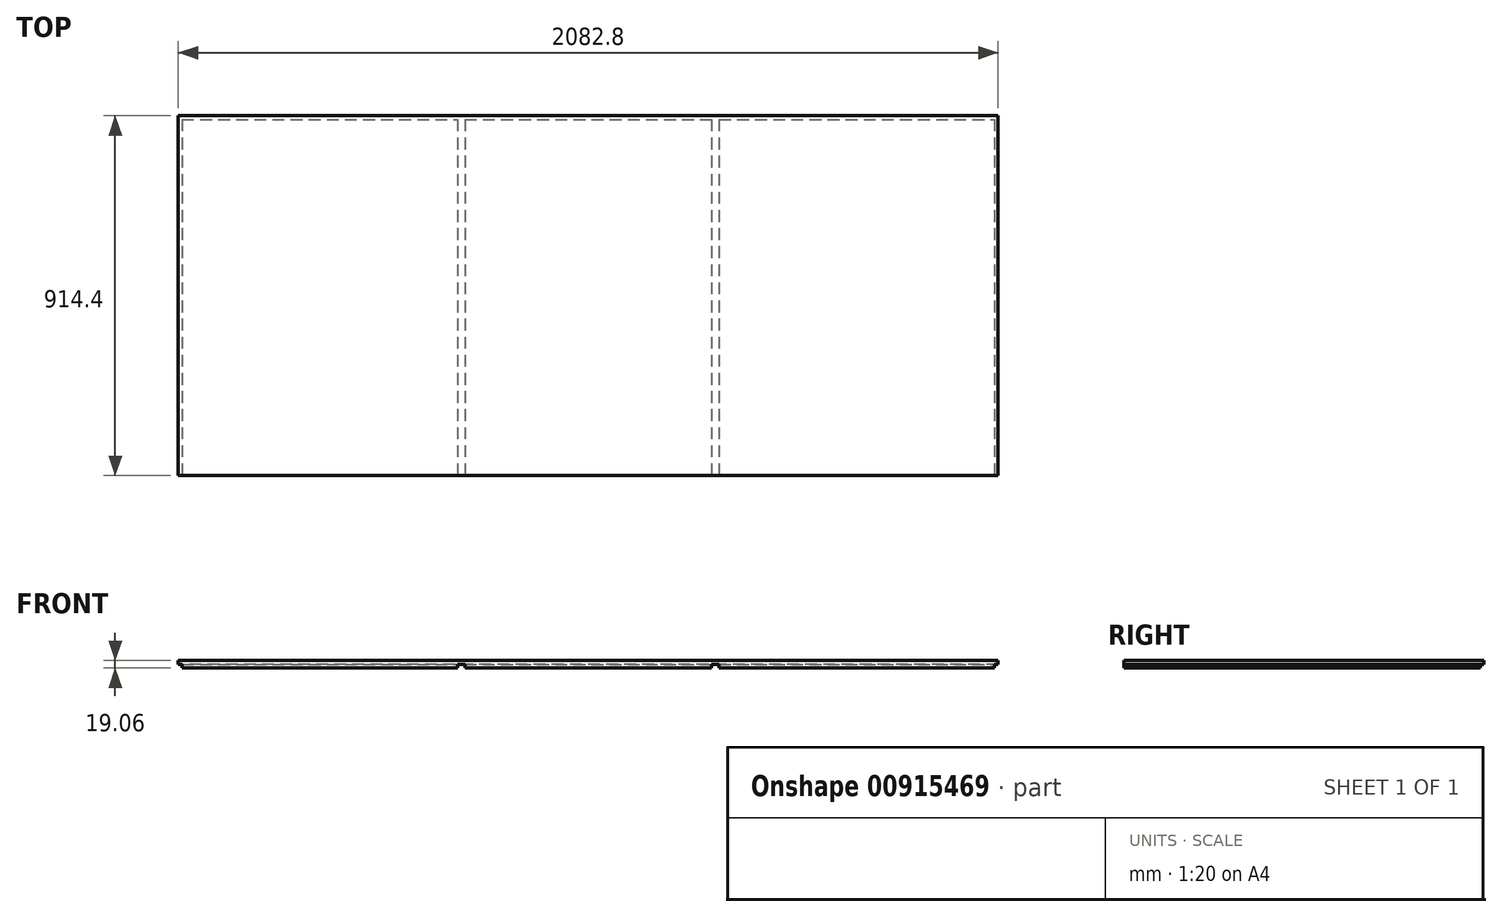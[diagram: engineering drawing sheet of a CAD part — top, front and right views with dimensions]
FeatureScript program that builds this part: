
annotation { "Feature Type Name" : "Feature", "Feature Type Description" : "" }
export const myFeature = defineFeature(function(context is Context, id is Id, definition is map)
    precondition{}
    {
        {
            var Q0;
            Q0=qCreatedBy(makeId("Top.planeOp"),FACE);
            var sketch = newSketch(context, id + "F0", { "sketchPlane" : qUnion([Q0])});
            skLineSegment(sketch, "E0.bottom", {"start": v(1041.4, 457.2) * mm, "end": v(-1041.4, 457.2) * mm});
            skLineSegment(sketch, "E0.top", {"start": v(1041.4, -457.2) * mm, "end": v(-1041.4, -457.2) * mm});
            skLineSegment(sketch, "E0.left", {"start": v(1041.4, 457.2) * mm, "end": v(1041.4, -457.2) * mm});
            skLineSegment(sketch, "E0.right", {"start": v(-1041.4, 457.2) * mm, "end": v(-1041.4, -457.2) * mm});
            skPoint(sketch, "E0.middle", {"position": v(0, 0) * mm});
            skSolve(sketch);
        }
        {
            var Q0;
            Q0=qCreatedBy(makeId("Top.planeOp"),FACE);
            var sketch = newSketch(context, id + "F1", { "sketchPlane" : qUnion([Q0])});
            skLineSegment(sketch, "E1.bottom", {"start": v(-1031.88, 447.68) * mm, "end": v(-332.32, 447.68) * mm});
            skLineSegment(sketch, "E1.top", {"start": v(-1031.88, -457.2) * mm, "end": v(-332.32, -457.2) * mm});
            skLineSegment(sketch, "E1.left", {"start": v(-1031.88, 447.68) * mm, "end": v(-1031.88, -457.2) * mm});
            skLineSegment(sketch, "E1.right", {"start": v(1031.88, 447.68) * mm, "end": v(1031.88, -457.2) * mm});
            skPoint(sketch, "E1.middle", {"position": v(0, -4.76) * mm});
            skLineSegment(sketch, "E2", {"start": v(313.27, 447.68) * mm, "end": v(313.27, -457.2) * mm});
            skLineSegment(sketch, "E3", {"start": v(332.32, 447.68) * mm, "end": v(332.32, -457.2) * mm});
            skLineSegment(sketch, "E4.trimOffspring", {"start": v(332.32, -457.2) * mm, "end": v(1031.88, -457.2) * mm});
            skLineSegment(sketch, "E5.trimOffspring", {"start": v(332.32, 447.68) * mm, "end": v(1031.88, 447.68) * mm});
            skLineSegment(sketch, "E6", {"start": v(-332.32, 447.68) * mm, "end": v(-332.32, -457.2) * mm});
            skLineSegment(sketch, "E7", {"start": v(-313.27, 447.68) * mm, "end": v(-313.27, -457.2) * mm});
            skLineSegment(sketch, "E8.trimOffspring", {"start": v(-313.27, 447.68) * mm, "end": v(313.27, 447.68) * mm});
            skLineSegment(sketch, "E9.trimOffspring", {"start": v(-313.27, -457.2) * mm, "end": v(313.27, -457.2) * mm});
            skSolve(sketch);
        }
        {
            var Q0;
            Q0=qSketchRegion(id+"F0",true);
            extrude(context, id + "F2", {"entities" : qUnion([Q0]), "depth" : 9.52 * mm, "offsetDistance" : 25.4 * mm});
        }
        {
            var Q0;
            Q0=qSketchRegion(id+"F1",true);
            extrude(context, id + "F3", {"entities" : qUnion([Q0]), "operationType" : NewBodyOperationType.ADD, "oppositeDirection" : true, "depth" : 9.52 * mm, "offsetDistance" : 25.4 * mm});
        }
    });
